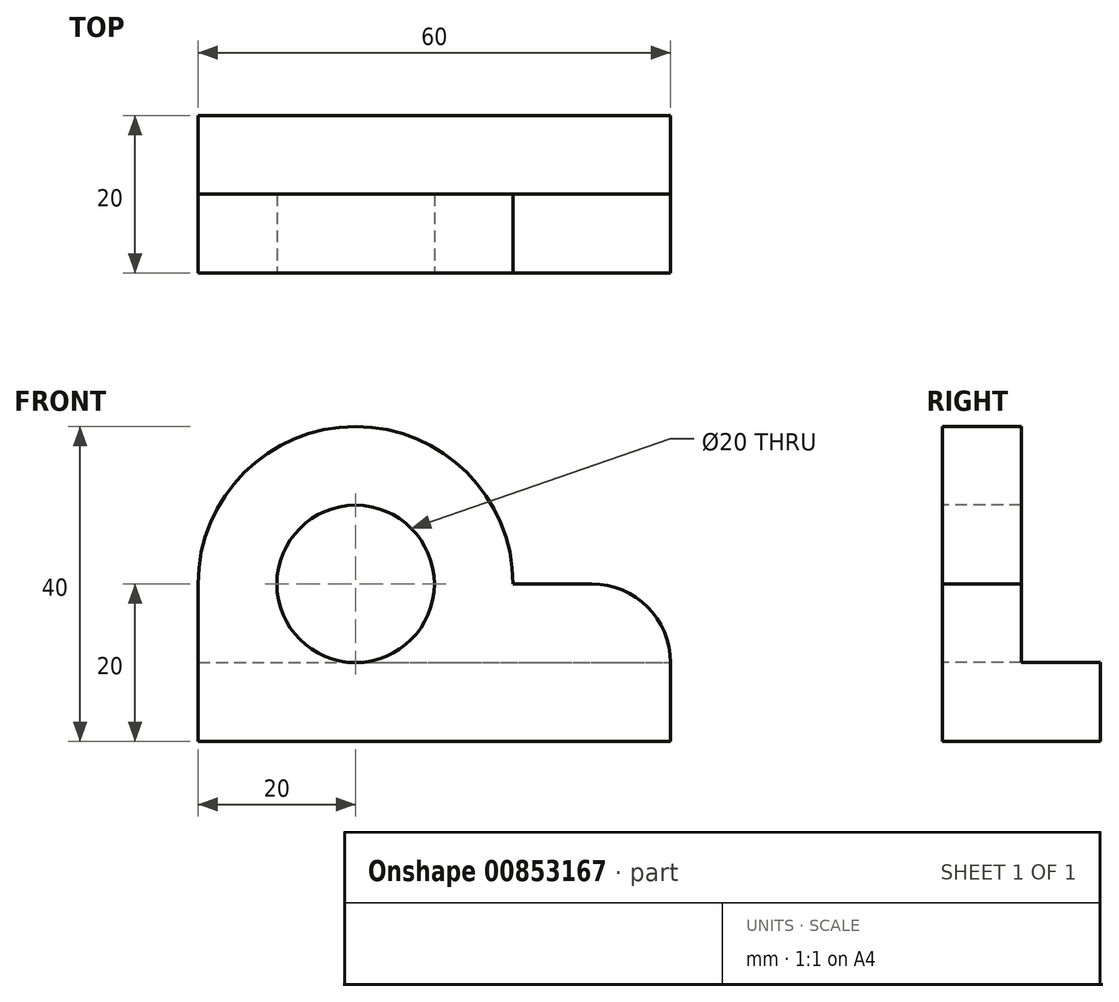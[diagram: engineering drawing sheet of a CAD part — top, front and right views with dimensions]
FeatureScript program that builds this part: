
annotation { "Feature Type Name" : "Feature", "Feature Type Description" : "" }
export const myFeature = defineFeature(function(context is Context, id is Id, definition is map)
    precondition{}
    {
        {
            var Q0;
            Q0=qCreatedBy(makeId("Front.planeOp"),FACE);
            var sketch = newSketch(context, id + "F0", { "sketchPlane" : qUnion([Q0])});
            skLineSegment(sketch, "E0.bottom", {"start": v(0, 0) * mm, "end": v(60, 0) * mm});
            skLineSegment(sketch, "E0.left", {"start": v(0, 0) * mm, "end": v(0, 20) * mm});
            skLineSegment(sketch, "E0.right", {"start": v(60, 0) * mm, "end": v(60, 10) * mm});
            skLineSegment(sketch, "E1.bottom", {"start": v(0, 0) * mm, "end": v(20, 0) * mm});
            skArc(sketch, "E2", {"start": v(40, 20) * mm, "mid": v(20, 40) * mm, "end": v(0, 20) * mm});
            skCircle(sketch, "E3", {"center": v(20, 20) * mm, "radius": 10 * mm});
            skPoint(sketch, "E4.visualSharp", {"position": v(60, 20) * mm});
            skArc(sketch, "E4.filletArc", {"start": v(60, 10) * mm, "mid": v(57.07, 17.07) * mm, "end": v(50, 20) * mm});
            skLineSegment(sketch, "E5.trimOffspring", {"start": v(40, 20) * mm, "end": v(50, 20) * mm});
            skSolve(sketch);
        }
        {
            var Q0;
            Q0=makeQuery(id+"F0.imprint","IMPRINT",FACE,{"disambiguationData":[TD([[makeQuery(id+"F0.imprint","IMPRINT",EDGE,{"derivedFrom":sQuery(id+"F0.wireOp",EDGE,"E0.bottom")}),1.0]])]});
            extrude(context, id + "F1", {"entities" : qUnion([Q0]), "oppositeDirection" : true, "depth" : 10 * mm, "offsetDistance" : 25 * mm});
        }
        {
            var Q0;
            Q0=makeQuery(id+"F1.opExtrude","CAP_FACE",FACE,{"disambiguationData":[OSD([sQuery(id+"F0.wireOp",EDGE,"E0.bottom"),sQuery(id+"F0.wireOp",EDGE,"E0.right"),sQuery(id+"F0.wireOp",EDGE,"E1.bottom"),sQuery(id+"F0.wireOp",EDGE,"E0.left"),sQuery(id+"F0.wireOp",EDGE,"E2"),sQuery(id+"F0.wireOp",EDGE,"E3"),sQuery(id+"F0.wireOp",EDGE,"E4.filletArc"),sQuery(id+"F0.wireOp",EDGE,"E5.trimOffspring")])],"isStart":false});
            var sketch = newSketch(context, id + "F2", { "sketchPlane" : qUnion([Q0])});
            skLineSegment(sketch, "E6.bottom", {"start": v(0, 0) * mm, "end": v(-60, 0) * mm});
            skLineSegment(sketch, "E6.top", {"start": v(0, 10) * mm, "end": v(-60, 10) * mm});
            skLineSegment(sketch, "E6.left", {"start": v(0, 0) * mm, "end": v(0, 10) * mm});
            skLineSegment(sketch, "E6.right", {"start": v(-60, 0) * mm, "end": v(-60, 10) * mm});
            skSolve(sketch);
        }
        {
            var Q0;
            Q0=makeQuery(id+"F2.imprint","IMPRINT",FACE,{"disambiguationData":[TD([[makeQuery(id+"F2.imprint","IMPRINT",EDGE,{"derivedFrom":sQuery(id+"F2.wireOp",EDGE,"E6.bottom")}),-1.0]])]});
            extrude(context, id + "F3", {"entities" : qUnion([Q0]), "operationType" : NewBodyOperationType.ADD, "depth" : 10 * mm, "offsetDistance" : 25 * mm});
        }
    });
